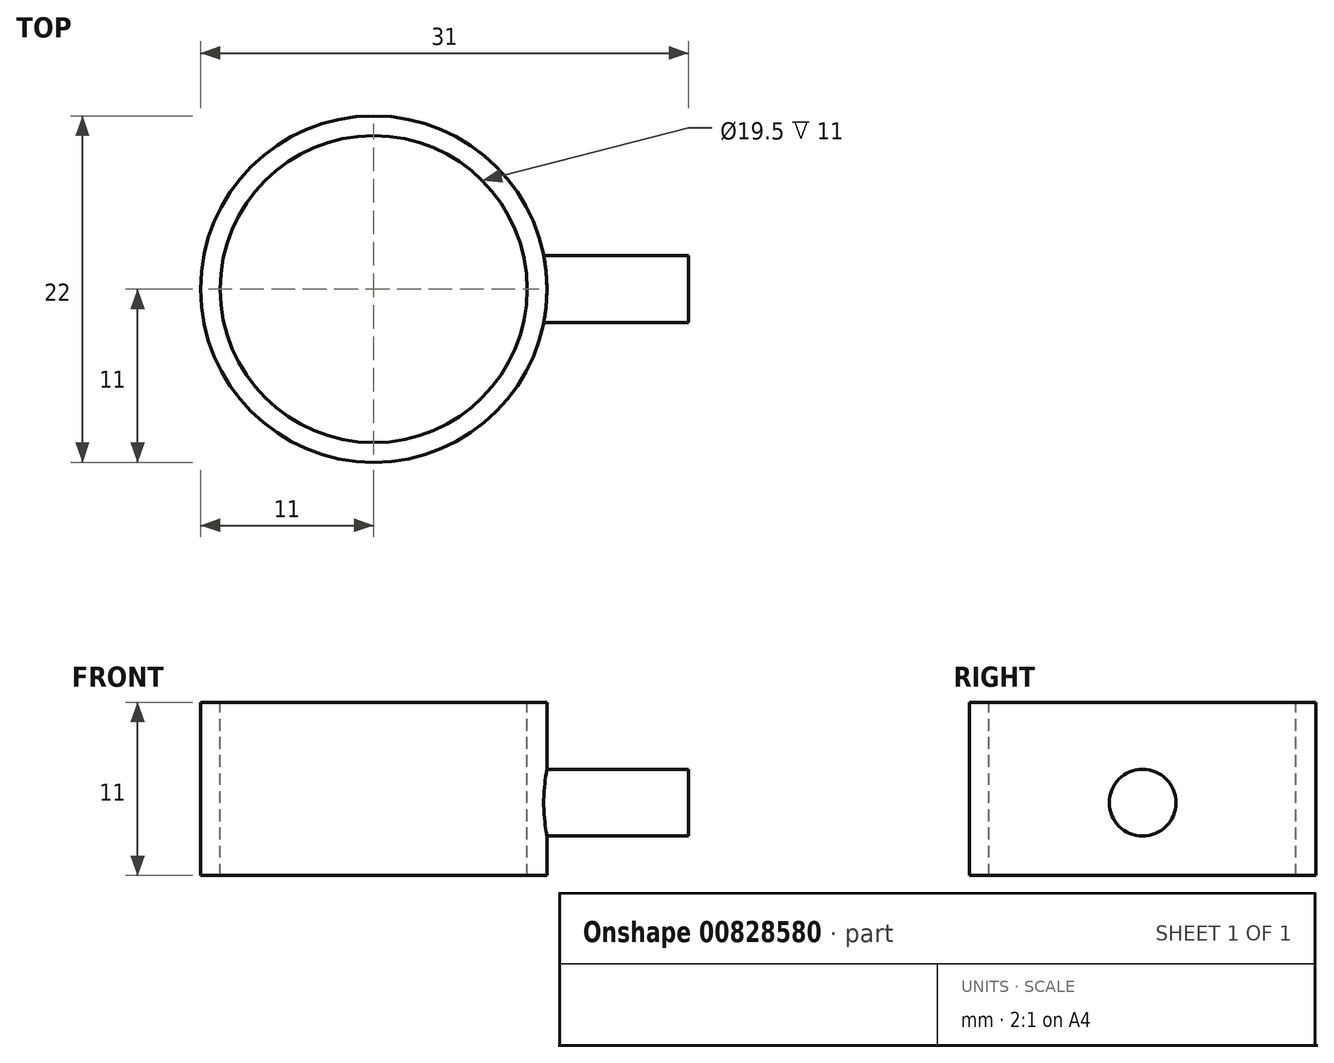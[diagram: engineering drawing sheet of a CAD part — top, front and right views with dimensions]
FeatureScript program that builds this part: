
annotation { "Feature Type Name" : "Feature", "Feature Type Description" : "" }
export const myFeature = defineFeature(function(context is Context, id is Id, definition is map)
    precondition{}
    {
        {
            var Q0;
            Q0=qCreatedBy(makeId("Top.planeOp"),FACE);
            var sketch = newSketch(context, id + "F0", { "sketchPlane" : qUnion([Q0])});
            skCircle(sketch, "E0", {"center": v(0, 0) * mm, "radius": 11 * mm});
            skSolve(sketch);
        }
        {
            var Q0;
            Q0=makeQuery(id+"F0.imprint","IMPRINT",FACE,{"disambiguationData":[TD([[makeQuery(id+"F0.imprint","IMPRINT",EDGE,{"derivedFrom":sQuery(id+"F0.wireOp",EDGE,"E0")}),1.0]])]});
            extrude(context, id + "F1", {"entities" : qUnion([Q0]), "depth" : 11 * mm, "offsetDistance" : 25.4 * mm});
        }
        {
            var Q0;
            Q0=makeQuery(id+"F1.opExtrude","CAP_FACE",FACE,{"disambiguationData":[OSD([sQuery(id+"F0.wireOp",EDGE,"E0")])],"isStart":false});
            var sketch = newSketch(context, id + "F2", { "sketchPlane" : qUnion([Q0])});
            skCircle(sketch, "E1", {"center": v(0, 0) * mm, "radius": 9.75 * mm});
            skSolve(sketch);
        }
        {
            var Q0;
            Q0=makeQuery(id+"F2.imprint","IMPRINT",FACE,{"disambiguationData":[TD([[makeQuery(id+"F2.imprint","IMPRINT",EDGE,{"derivedFrom":sQuery(id+"F2.wireOp",EDGE,"E1")}),1.0]])]});
            extrude(context, id + "F3", {"entities" : qUnion([Q0]), "operationType" : NewBodyOperationType.REMOVE, "oppositeDirection" : true, "depth" : 11 * mm, "offsetDistance" : 25.4 * mm});
        }
        {
            var Q0;
            Q0=qCreatedBy(makeId("Right.planeOp"),FACE);
            cPlane(context, id + "F4", {"entities" : qUnion([Q0]), "cplaneType" : CPlaneType.OFFSET, "offset" : 10 * mm, "width" : 152.4 * mm, "height" : 152.4 * mm});
        }
        {
            var Q0;
            Q0=qCreatedBy(id+"F4.planeOp",FACE);
            var sketch = newSketch(context, id + "F5", { "sketchPlane" : qUnion([Q0])});
            skCircle(sketch, "E2", {"center": v(0, 4.63) * mm, "radius": 2.12 * mm});
            skSolve(sketch);
        }
        {
            var Q0;
            Q0=makeQuery(id+"F5.imprint","IMPRINT",FACE,{"disambiguationData":[TD([[makeQuery(id+"F5.imprint","IMPRINT",EDGE,{"derivedFrom":sQuery(id+"F5.wireOp",EDGE,"E2")}),1.0]])]});
            extrude(context, id + "F6", {"entities" : qUnion([Q0]), "operationType" : NewBodyOperationType.ADD, "depth" : 10 * mm, "offsetDistance" : 25.4 * mm});
        }
    });
